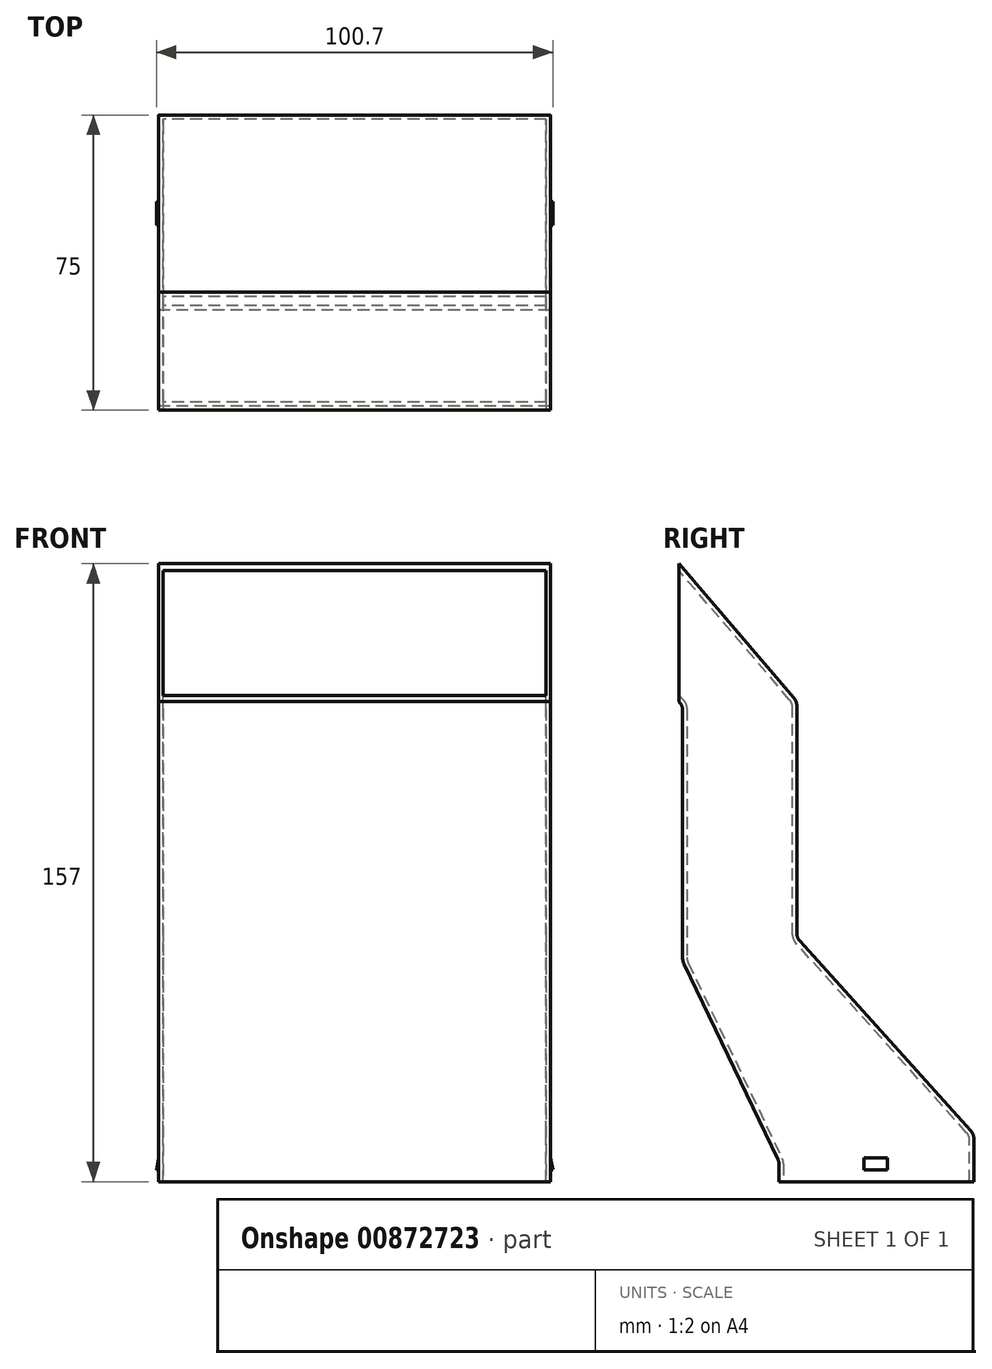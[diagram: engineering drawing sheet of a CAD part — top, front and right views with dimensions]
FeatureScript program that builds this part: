
annotation { "Feature Type Name" : "Feature", "Feature Type Description" : "" }
export const myFeature = defineFeature(function(context is Context, id is Id, definition is map)
    precondition{}
    {
        {
            var Q0;
            Q0=qCreatedBy(makeId("Right.planeOp"),FACE);
            var sketch = newSketch(context, id + "F0", { "sketchPlane" : qUnion([Q0])});
            skLineSegment(sketch, "E0", {"start": v(0, 0) * mm, "end": v(0, 12) * mm});
            skLineSegment(sketch, "E1", {"start": v(0, 12) * mm, "end": v(-45, 62) * mm});
            skLineSegment(sketch, "E2", {"start": v(-45, 62) * mm, "end": v(-45, 122) * mm});
            skLineSegment(sketch, "E3", {"start": v(-74, 121) * mm, "end": v(-74, 56) * mm});
            skLineSegment(sketch, "E4", {"start": v(-74, 56) * mm, "end": v(-49.5, 5) * mm});
            skLineSegment(sketch, "E5", {"start": v(-49.5, 5) * mm, "end": v(-49.5, 0) * mm});
            skLineSegment(sketch, "E6", {"start": v(-49.5, 0) * mm, "end": v(0, 0) * mm});
            skLineSegment(sketch, "E7", {"start": v(-45, 122) * mm, "end": v(-75, 157) * mm});
            skLineSegment(sketch, "E8", {"start": v(-74, 121) * mm, "end": v(-75, 122) * mm});
            skLineSegment(sketch, "E9", {"start": v(-75, 157) * mm, "end": v(-75, 122) * mm});
            skSolve(sketch);
        }
        {
            var Q0;
            Q0=makeQuery(id+"F0.imprint","IMPRINT",FACE,{"disambiguationData":[TD([[makeQuery(id+"F0.imprint","IMPRINT",EDGE,{"derivedFrom":sQuery(id+"F0.wireOp",EDGE,"E0")}),1.0]])]});
            extrude(context, id + "F1", {"entities" : qUnion([Q0]), "depth" : 99.5 * mm, "offsetDistance" : 25 * mm});
        }
        {
            var Q0;
            Q0=makeQuery(id+"F1.opExtrude","SWEPT_FACE",FACE,{"disambiguationData":[OSD([sQuery(id+"F0.wireOp",EDGE,"E9")])]});
            var Q1;
            Q1=makeQuery(id+"F1.opExtrude","SWEPT_FACE",FACE,{"disambiguationData":[OSD([sQuery(id+"F0.wireOp",EDGE,"E6")])]});
            shell(context, id + "F2", {"entities" : qUnion([Q0, Q1]), "thickness" : 1.1 * mm});
        }
        {
            var Q0;
            Q0=makeQuery(id+"F1.opExtrude","SWEPT_EDGE",EDGE,{"disambiguationData":[OSD([sQuery(id+"F0.wireOp",EDGE,"E3"),sQuery(id+"F0.wireOp",EDGE,"E8")])]});
            var Q1;
            Q1=makeQuery(id+"F1.opExtrude","SWEPT_EDGE",EDGE,{"disambiguationData":[OSD([sQuery(id+"F0.wireOp",EDGE,"E3"),sQuery(id+"F0.wireOp",EDGE,"E4")])]});
            var Q2;
            Q2=makeQuery(id+"F1.opExtrude","SWEPT_EDGE",EDGE,{"disambiguationData":[OSD([sQuery(id+"F0.wireOp",EDGE,"E4"),sQuery(id+"F0.wireOp",EDGE,"E5")])]});
            var Q3;
            Q3=makeQuery(id+"F1.opExtrude","SWEPT_EDGE",EDGE,{"disambiguationData":[OSD([sQuery(id+"F0.wireOp",EDGE,"E0"),sQuery(id+"F0.wireOp",EDGE,"E1")])]});
            var Q4;
            Q4=makeQuery(id+"F1.opExtrude","SWEPT_EDGE",EDGE,{"disambiguationData":[OSD([sQuery(id+"F0.wireOp",EDGE,"E1"),sQuery(id+"F0.wireOp",EDGE,"E2")])]});
            var Q5;
            Q5=makeQuery(id+"F1.opExtrude","SWEPT_EDGE",EDGE,{"disambiguationData":[OSD([sQuery(id+"F0.wireOp",EDGE,"E2"),sQuery(id+"F0.wireOp",EDGE,"E7")])]});
            var Q6;
            Q6=makeQuery(id+"F2.opShell","OFFSET_EDGE",EDGE,{"disambiguationData":[OSD([sQuery(id+"F0.wireOp",EDGE,"E0"),sQuery(id+"F0.wireOp",EDGE,"E1")])]});
            var Q7;
            Q7=makeQuery(id+"F2.opShell","OFFSET_EDGE",EDGE,{"disambiguationData":[OSD([sQuery(id+"F0.wireOp",EDGE,"E1"),sQuery(id+"F0.wireOp",EDGE,"E2")])]});
            var Q8;
            Q8=makeQuery(id+"F2.opShell","OFFSET_EDGE",EDGE,{"disambiguationData":[OSD([sQuery(id+"F0.wireOp",EDGE,"E3"),sQuery(id+"F0.wireOp",EDGE,"E4")])]});
            var Q9;
            Q9=makeQuery(id+"F2.opShell","OFFSET_EDGE",EDGE,{"disambiguationData":[OSD([sQuery(id+"F0.wireOp",EDGE,"E2"),sQuery(id+"F0.wireOp",EDGE,"E7")])]});
            var Q10;
            Q10=makeQuery(id+"F2.opShell","OFFSET_EDGE",EDGE,{"disambiguationData":[OSD([sQuery(id+"F0.wireOp",EDGE,"E3"),sQuery(id+"F0.wireOp",EDGE,"E8")])]});
            var Q11;
            Q11=makeQuery(id+"F2.opShell","OFFSET_EDGE",EDGE,{"disambiguationData":[OSD([sQuery(id+"F0.wireOp",EDGE,"E4"),sQuery(id+"F0.wireOp",EDGE,"E5")])]});
            fillet(context, id + "F3", {"entities" : qUnion([Q0, Q1, Q2, Q3, Q4, Q5, Q6, Q7, Q8, Q9, Q10, Q11]), "radius" : 3 * mm, "tangentPropagation" : true, "allowEdgeOverflow" : false});
        }
        {
            var Q0;
            Q0=makeQuery(id+"F1.opExtrude","CAP_FACE",FACE,{"disambiguationData":[OSD([sQuery(id+"F0.wireOp",EDGE,"E0"),sQuery(id+"F0.wireOp",EDGE,"E1"),sQuery(id+"F0.wireOp",EDGE,"E2"),sQuery(id+"F0.wireOp",EDGE,"E3"),sQuery(id+"F0.wireOp",EDGE,"E4"),sQuery(id+"F0.wireOp",EDGE,"E5"),sQuery(id+"F0.wireOp",EDGE,"E6"),sQuery(id+"F0.wireOp",EDGE,"E7"),sQuery(id+"F0.wireOp",EDGE,"E8"),sQuery(id+"F0.wireOp",EDGE,"E9")])],"isStart":true});
            var sketch = newSketch(context, id + "F4", { "sketchPlane" : qUnion([Q0])});
            skLineSegment(sketch, "E10.bottom", {"start": v(22, 3) * mm, "end": v(28, 3) * mm});
            skLineSegment(sketch, "E10.top", {"start": v(22, 6) * mm, "end": v(28, 6) * mm});
            skLineSegment(sketch, "E10.left", {"start": v(22, 3) * mm, "end": v(22, 6) * mm});
            skLineSegment(sketch, "E10.right", {"start": v(28, 3) * mm, "end": v(28, 6) * mm});
            skSolve(sketch);
        }
        {
            var Q0;
            Q0 = qSketchRegion(id + "F4", true);
            extrude(context, id + "F5", {"entities" : qUnion([Q0]), "operationType" : NewBodyOperationType.ADD, "depth" : 1 * mm, "offsetDistance" : 25 * mm});
        }
        {
            var Q0;
            Q0=makeQuery(id+"F5.opExtrude","CAP_EDGE",EDGE,{"disambiguationData":[OSD([sQuery(id+"F4.wireOp",EDGE,"E10.top")])],"isStart":false});
            chamfer(context, id + "F6", {"entities" : qUnion([Q0]), "chamferType" : ChamferType.TWO_OFFSETS, "width1" : 1 * mm, "oppositeDirection" : false, "width2" : 5 * mm, "tangentPropagation" : true});
        }
        {
            var Q0;
            Q0=makeQuery(id+"F1.opExtrude","CAP_FACE",FACE,{"disambiguationData":[OSD([sQuery(id+"F0.wireOp",EDGE,"E0"),sQuery(id+"F0.wireOp",EDGE,"E1"),sQuery(id+"F0.wireOp",EDGE,"E2"),sQuery(id+"F0.wireOp",EDGE,"E3"),sQuery(id+"F0.wireOp",EDGE,"E4"),sQuery(id+"F0.wireOp",EDGE,"E5"),sQuery(id+"F0.wireOp",EDGE,"E6"),sQuery(id+"F0.wireOp",EDGE,"E7"),sQuery(id+"F0.wireOp",EDGE,"E8"),sQuery(id+"F0.wireOp",EDGE,"E9")])],"isStart":false});
            var sketch = newSketch(context, id + "F7", { "sketchPlane" : qUnion([Q0])});
            skLineSegment(sketch, "E11.bottom", {"start": v(-28, 6) * mm, "end": v(-22, 6) * mm});
            skLineSegment(sketch, "E11.top", {"start": v(-28, 3) * mm, "end": v(-22, 3) * mm});
            skLineSegment(sketch, "E11.left", {"start": v(-28, 6) * mm, "end": v(-28, 3) * mm});
            skLineSegment(sketch, "E11.right", {"start": v(-22, 6) * mm, "end": v(-22, 3) * mm});
            skSolve(sketch);
        }
        {
            var Q0;
            Q0 = qSketchRegion(id + "F7", true);
            extrude(context, id + "F8", {"entities" : qUnion([Q0]), "operationType" : NewBodyOperationType.ADD, "depth" : 1 * mm, "offsetDistance" : 25 * mm});
        }
        {
            var Q0;
            Q0=makeQuery(id+"F8.opExtrude","CAP_EDGE",EDGE,{"disambiguationData":[OSD([sQuery(id+"F7.wireOp",EDGE,"E11.bottom")])],"isStart":false});
            chamfer(context, id + "F9", {"entities" : qUnion([Q0]), "chamferType" : ChamferType.TWO_OFFSETS, "width1" : 1 * mm, "oppositeDirection" : false, "width2" : 5 * mm, "tangentPropagation" : true});
        }
    });
